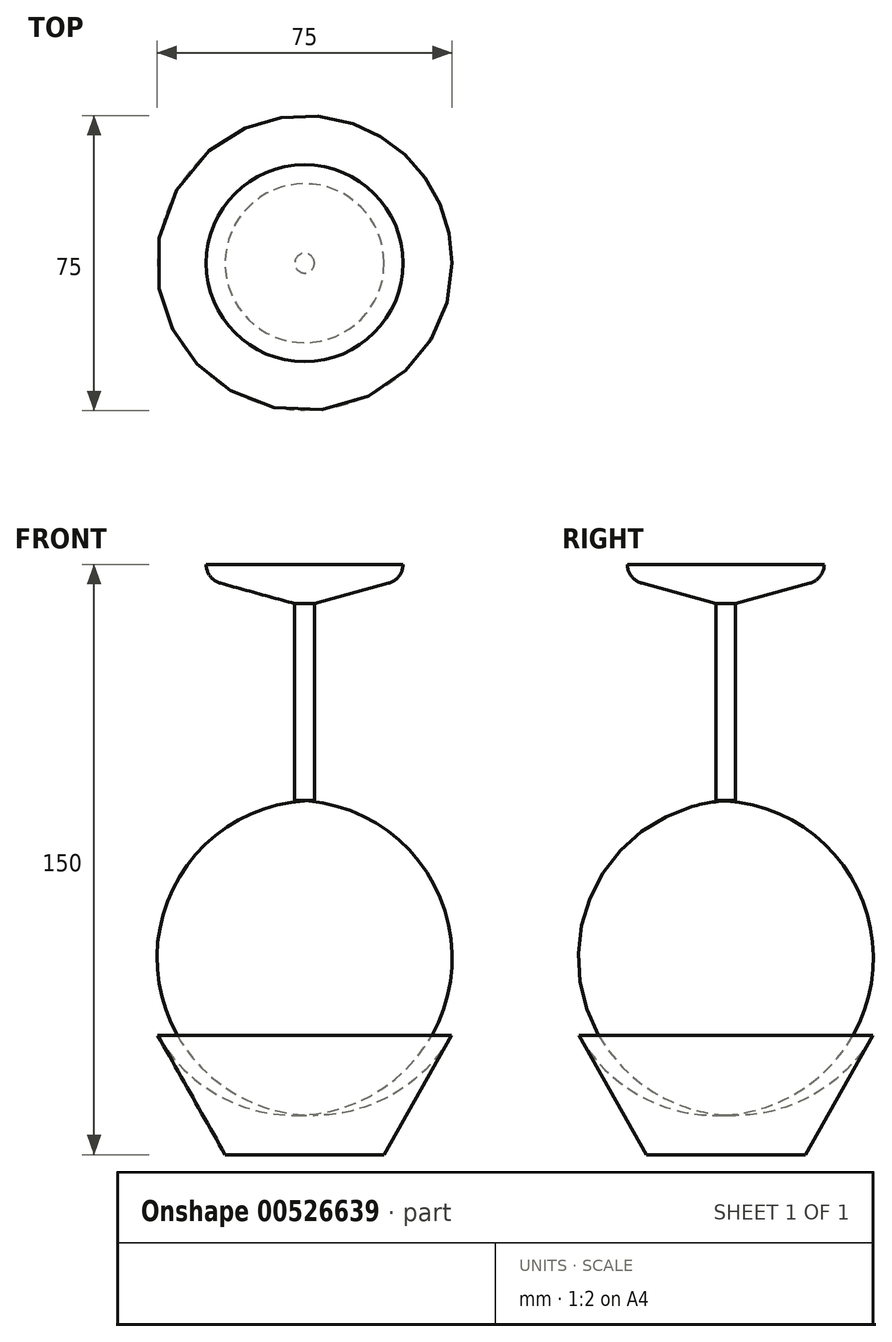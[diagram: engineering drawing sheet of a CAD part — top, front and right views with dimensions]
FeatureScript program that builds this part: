
annotation { "Feature Type Name" : "Feature", "Feature Type Description" : "" }
export const myFeature = defineFeature(function(context is Context, id is Id, definition is map)
    precondition{}
    {
        {
            var Q0;
            Q0=qCreatedBy(makeId("Front.planeOp"),FACE);
            var sketch = newSketch(context, id + "F0", { "sketchPlane" : qUnion([Q0])});
            skLineSegment(sketch, "E0", {"start": v(0, 0) * mm, "end": v(25, 0) * mm});
            skArc(sketch, "E1", {"start": v(25, 0) * mm, "mid": v(23.98, -3.03) * mm, "end": v(21.33, -4.82) * mm});
            skLineSegment(sketch, "E2", {"start": v(21.33, -4.82) * mm, "end": v(2.5, -10) * mm});
            skLineSegment(sketch, "E3", {"start": v(2.5, -10) * mm, "end": v(2.5, -60) * mm});
            skArc(sketch, "E4", {"start": v(2.5, -60) * mm, "mid": v(37.05, -79.84) * mm, "end": v(37.33, -119.67) * mm});
            skLineSegment(sketch, "E5", {"start": v(37.33, -119.67) * mm, "end": v(20.2, -150) * mm});
            skLineSegment(sketch, "E6", {"start": v(20.2, -150) * mm, "end": v(0, -150) * mm});
            skLineSegment(sketch, "E7", {"start": v(0, -150) * mm, "end": v(0, 0) * mm});
            skSolve(sketch);
        }
        {
            var Q0;
            Q0=makeQuery(id+"F0.imprint","IMPRINT",FACE,{"disambiguationData":[TD([[makeQuery(id+"F0.imprint","IMPRINT",EDGE,{"derivedFrom":sQuery(id+"F0.wireOp",EDGE,"E0")}),-1.0]])]});
            var Q1;
            Q1=sQuery(id+"F0.wireOp",EDGE,"E7");
            revolve(context, id + "F1", {"entities" : qUnion([Q0]), "axis" : qUnion([Q1]), "revolveType" : RevolveType.FULL});
        }
    });
